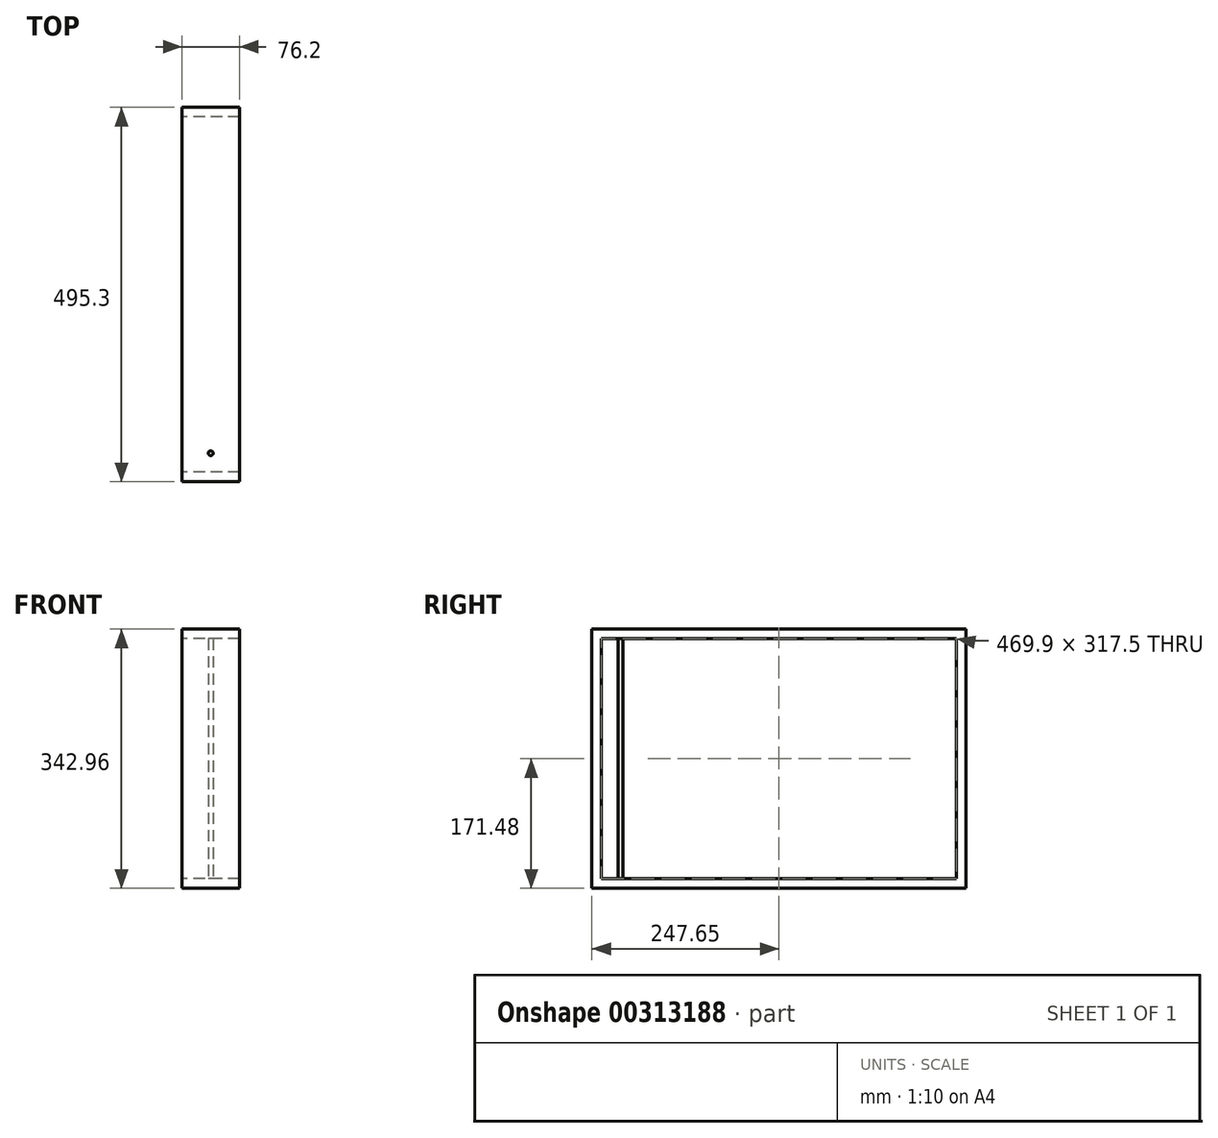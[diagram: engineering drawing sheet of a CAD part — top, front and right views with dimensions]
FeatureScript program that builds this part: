
annotation { "Feature Type Name" : "Feature", "Feature Type Description" : "" }
export const myFeature = defineFeature(function(context is Context, id is Id, definition is map)
    precondition{}
    {
        {
            var Q0;
            Q0=qCreatedBy(makeId("Right.planeOp"),FACE);
            var sketch = newSketch(context, id + "F0", { "sketchPlane" : qUnion([Q0])});
            skLineSegment(sketch, "E0.bottom", {"start": v(-247.65, -171.45) * mm, "end": v(247.65, -171.45) * mm});
            skLineSegment(sketch, "E0.top", {"start": v(-247.65, 171.45) * mm, "end": v(247.65, 171.45) * mm});
            skLineSegment(sketch, "E0.left", {"start": v(-247.65, -171.45) * mm, "end": v(-247.65, 171.45) * mm});
            skLineSegment(sketch, "E0.right", {"start": v(247.65, -171.45) * mm, "end": v(247.65, 171.45) * mm});
            skPoint(sketch, "E0.middle", {"position": v(0, 0) * mm});
            skLineSegment(sketch, "E1.bottom", {"start": v(-234.95, -158.75) * mm, "end": v(234.95, -158.75) * mm});
            skLineSegment(sketch, "E1.top", {"start": v(-234.95, 158.75) * mm, "end": v(234.95, 158.75) * mm});
            skLineSegment(sketch, "E1.left", {"start": v(-234.95, -158.75) * mm, "end": v(-234.95, 158.75) * mm});
            skLineSegment(sketch, "E1.right", {"start": v(234.95, -158.75) * mm, "end": v(234.95, 158.75) * mm});
            skSolve(sketch);
        }
        {
            var Q0;
            Q0 = qSketchRegion(id + "F0", true);
            extrude(context, id + "F1", {"entities" : qUnion([Q0]), "endBound" : BoundingType.SYMMETRIC, "depth" : 76.2 * mm});
        }
        {
            var Q0;
            Q0=qCreatedBy(makeId("Top.planeOp"),FACE);
            var sketch = newSketch(context, id + "F2", { "sketchPlane" : qUnion([Q0])});
            skLineSegment(sketch, "E2", {"start": v(0, -247.98) * mm, "end": v(0, -209.88) * mm, "construction": true});
            skCircle(sketch, "E3", {"center": v(0, -209.88) * mm, "radius": 3.18 * mm});
            skSolve(sketch);
        }
        {
            var Q0;
            Q0 = qSketchRegion(id + "F2", true);
            extrude(context, id + "F3", {"entities" : qUnion([Q0]), "operationType" : NewBodyOperationType.ADD, "depth" : 171.48 * mm, "hasSecondDirection" : true, "secondDirectionOppositeDirection" : true, "secondDirectionDepth" : 171.48 * mm});
        }
    });
